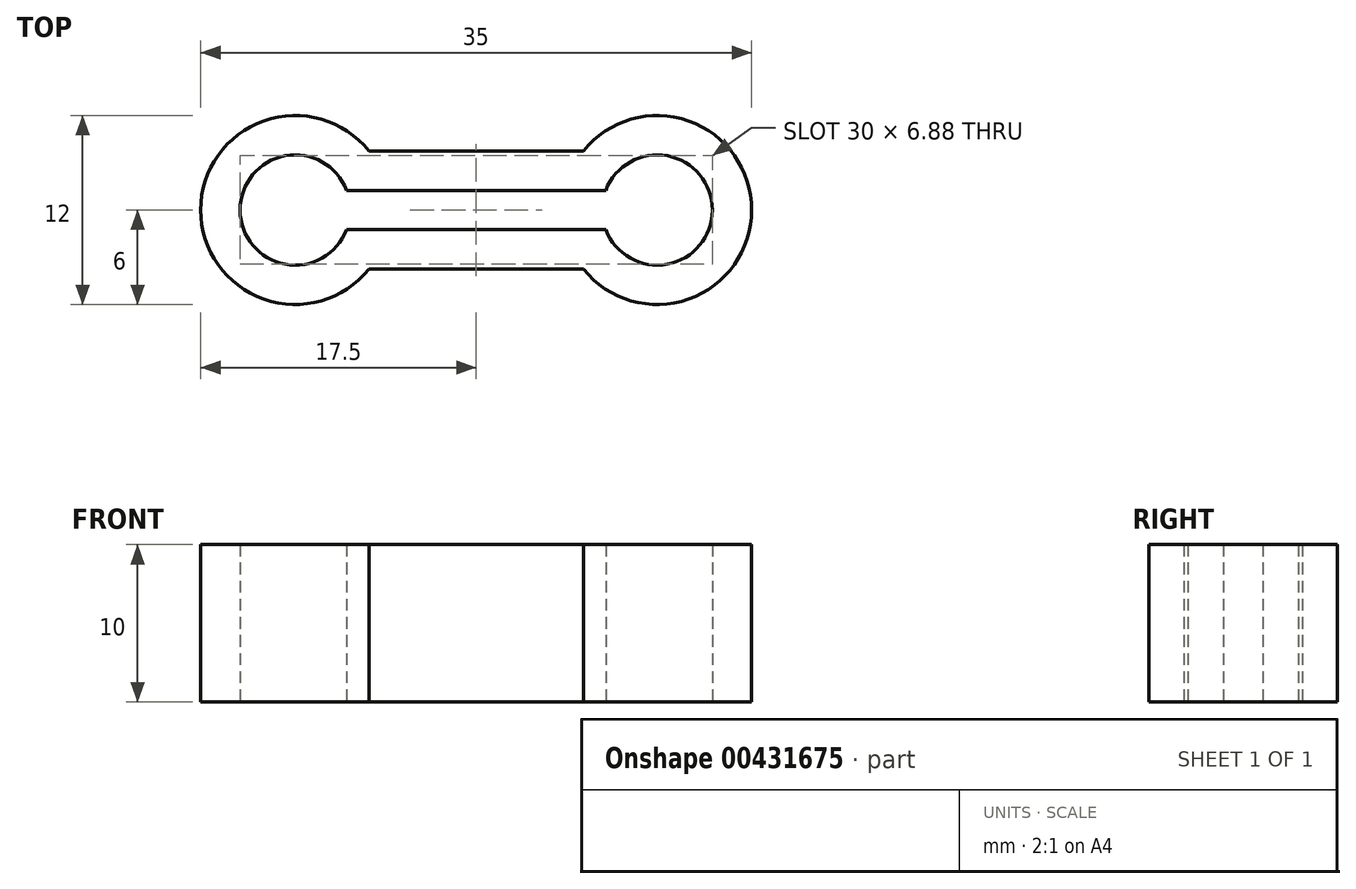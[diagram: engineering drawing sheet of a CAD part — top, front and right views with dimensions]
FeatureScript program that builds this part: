
annotation { "Feature Type Name" : "Feature", "Feature Type Description" : "" }
export const myFeature = defineFeature(function(context is Context, id is Id, definition is map)
    precondition{}
    {
        {
            var Q0;
            Q0=qCreatedBy(makeId("Top.planeOp"),FACE);
            var sketch = newSketch(context, id + "F0", { "sketchPlane" : qUnion([Q0])});
            skArc(sketch, "E0", {"start": v(6.82, -3.75) * mm, "mid": v(17.5, 0) * mm, "end": v(6.82, 3.75) * mm});
            skLineSegment(sketch, "E1", {"start": v(6.82, 3.75) * mm, "end": v(0, 3.75) * mm});
            skLineSegment(sketch, "E2", {"start": v(5.5, 0) * mm, "end": v(0, 0) * mm, "construction": true});
            skLineSegment(sketch, "E3", {"start": v(0, -3.75) * mm, "end": v(6.82, -3.75) * mm});
            skLineSegment(sketch, "E4", {"start": v(0, 3.75) * mm, "end": v(0, -3.75) * mm});
            skLineSegment(sketch, "E5.0", {"start": v(8.23, 1.25) * mm, "end": v(0, 1.25) * mm});
            skArc(sketch, "E5.1", {"start": v(8.23, -1.25) * mm, "mid": v(15, 0) * mm, "end": v(8.23, 1.25) * mm});
            skLineSegment(sketch, "E5.2", {"start": v(0, -1.25) * mm, "end": v(8.23, -1.25) * mm});
            skSolve(sketch);
        }
        {
            var Q0;
            {var subQ0=sQuery(id+"F0.wireOp",EDGE,"E1");Q0=makeQuery(id+"F0.imprint","IMPRINT",FACE,{"disambiguationData":[TD([[makeQuery(id+"F0.imprint","IMPRINT",EDGE,{"derivedFrom":subQ0}),1.0]])]});}
            var Q1;
            {var subQ0=sQuery(id+"F0.wireOp",EDGE,"E0");var subQ1=makeQuery(id+"F0.imprint","INTERSECT",VERTEX,{"derivedFrom":[subQ0,sQuery(id+"F0.wireOp",EDGE,"E1")]});Q1=makeQuery(id+"F0.imprint","IMPRINT",FACE,{"disambiguationData":[TD([[makeQuery(id+"F0.imprint","IMPRINT",EDGE,{"disambiguationData":[TD([[subQ1,-1.0]])],"derivedFrom":subQ0}),1.0]])]});}
            extrude(context, id + "F1", {"entities" : qUnion([Q0, Q1]), "endBound" : BoundingType.SYMMETRIC, "depth" : 10 * mm});
        }
        {
            var Q0;
            Q0=makeQuery(id+"F1.opExtrude","SWEPT_BODY",BODY,{"disambiguationData":[OSD([sQuery(id+"F0.wireOp",EDGE,"E0"),sQuery(id+"F0.wireOp",EDGE,"E1"),sQuery(id+"F0.wireOp",EDGE,"E3"),sQuery(id+"F0.wireOp",EDGE,"E4")])]});
            var Q1;
            Q1=qCreatedBy(makeId("Right.planeOp"),FACE);
            mirror(context, id + "F2", {"operationType" : NewBodyOperationType.ADD, "entities" : qUnion([Q0]), "mirrorPlane" : qUnion([Q1])});
        }
    });
